# Revit family: LeL Tago 3.3
name_source: partatom
category: Lighting Fixtures
units: mm (PartAtom-declared; Revit-internal decimal feet)

## family parameters
Always vertical = No
Cut with Voids When Loaded = No
Light Source = No
OmniClass Number = 23.80.70.00
OmniClass Title = Lighting
Part Type = Normal
Room Calculation Point = No
Round Connector Dimension = Use Diameter
Shared = No
Work Plane-Based = Yes

## types (7) — shared parameters
Apparent Load = 51 VA
CCT = 3000 K
CRI = CRI80
Default Elevation = 1219 mm
Description = Outdoor/linear profiles
Finish = LeL Black
IK = IK09
IP = IP65 IP67 IP69
Lamp = LED
Manufacturer = L&L Luce&Light srl
Model = TG33
Rated Power supply = 230 V
URL = https://www.lucelight.it
Wattage = 51 W
Weight = 3.60 kg

## per-type parameters (varying)
| type | Lumen Output | Optic |
| 3.3 A 51W | 2656 lm | TAGO Light source : 3.3 A 51W |
| 3.3 G 51W | 2730 lm | TAGO Light source : 3.3 G 51W |
| 3.3 K 69° 51W | 3768 lm | TAGO Light source : 3.3 K 69° 51W |
| 3.3 L 29° 51W | 3728 lm | TAGO Light source : 3.3 L 29° 51W |
| 3.3 M 17° 51W | 3355 lm | TAGO Light source : 3.3 M 17° 51W |
| 3.3 S 11° 51W | 2956 lm | TAGO Light source : 3.3 S 11° 51W |
| 3.3 W 20°x49° 51W | 3404 lm | TAGO Light source : 3.3 W 20°x49° 51W |

## geometry (parser evidence)
native form markers: Sweep x4
no freeform markers — native parametric forms only
